# Revit family: Tub_Spout-American_Standard-Times_Square-8888.097.002
name_source: partatom
category: Plumbing Fixtures
revit_build: Autodesk Revit 2018 (Build: 20170223_1515(x64)
units: mm (PartAtom-declared; Revit-internal decimal feet)

## family parameters
Cut with Voids When Loaded = No
Host = Face
OmniClass Number = 23.45.05.14.17
OmniClass Title = Showers
Part Type = Normal
Room Calculation Point = No
Round Connector Dimension = Use Radius
Shared = Yes

## types (1)
- 8888.097.002
    ADA Compliant = Yes
    Assembly Code = D2020300
    Body Material = Brass-American_Standard-002-Polished_Chrome
    CW Connection = Yes
    CWFU = 3
    Default Elevation = 0"
    Description = Times Square™ Slip-On Diverter Tub Spout
    HW Connection = Yes
    HWFU = 3
    Installation Type = Wall Mounted
    Length = 4 7/8"
    Manufacturer = American Standard
    Model = 8888.097.002
    Price = Prices may vary. Please consult Manufacturer Representative for most up-to-date price list.
    Product Documentation Link = https://www.americanstandard-us.com
    Product Page URL = https://www.americanstandard-us.com
    Tempered Water Connection Diameter = 1/2"
    Tempered Water Connection Radius = 1/4"
    URL = http://www.americanstandard-us.com
    Vent Connection = No
    WFU = 0
    Warranty Information = Limited Lifetime Function and Finish Warranty.
    Waste Connection = No
    Width = 3"

## geometry (parser evidence)
native form markers: Sweep x3
no freeform markers — native parametric forms only
